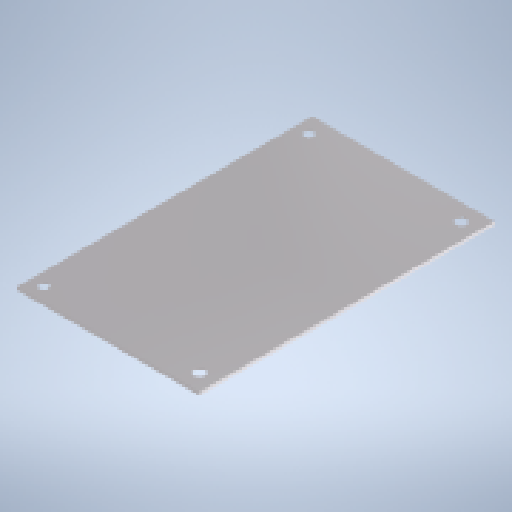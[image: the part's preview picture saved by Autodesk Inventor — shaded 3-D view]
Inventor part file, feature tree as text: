
AUTODESK INVENTOR PART (.ipt)
format: ipt  version: 2025 (Build 290162010, 162A)  size: 165,888 bytes
history: native  units: mm
features: hole x2, sketch x2, other x1
ambient origin geometry x8: Origin, YZ Plane, XZ Plane, XY Plane, X Axis, Y Axis, Z Axis, Center Point
bodies: Volumenkörper1 (feature_tree)
feature tree (5):
  hole  "Bohrung1"  [1 undecoded]
  hole  "Bohrung2"  [1 undecoded]
  sketch  "Skizze1"  dims[d1=10.0mm]
  sketch  "Skizze2"  dims[d2=5.3mm d3=6.0mm d4=10.4mm d5=2.0mm d6=90.0deg d7=8.0mm d8=20.594885mm d9=8.0mm d10=8.0mm d11=10.0mm d12=3.2mm d13=6.0mm d14=6.3mm d15=2.0mm d16=90.0deg d17=8.0mm d18=20.594885mm]
  other  "item_47308_blech-al-2mm-naturfarben_178_110_high_1_1:1"
note: 2 required parameter values undecoded (feature->parameter linkage not recoverable at this tier; creation-order binding heuristic only, values carry confidence <= 0.55)
